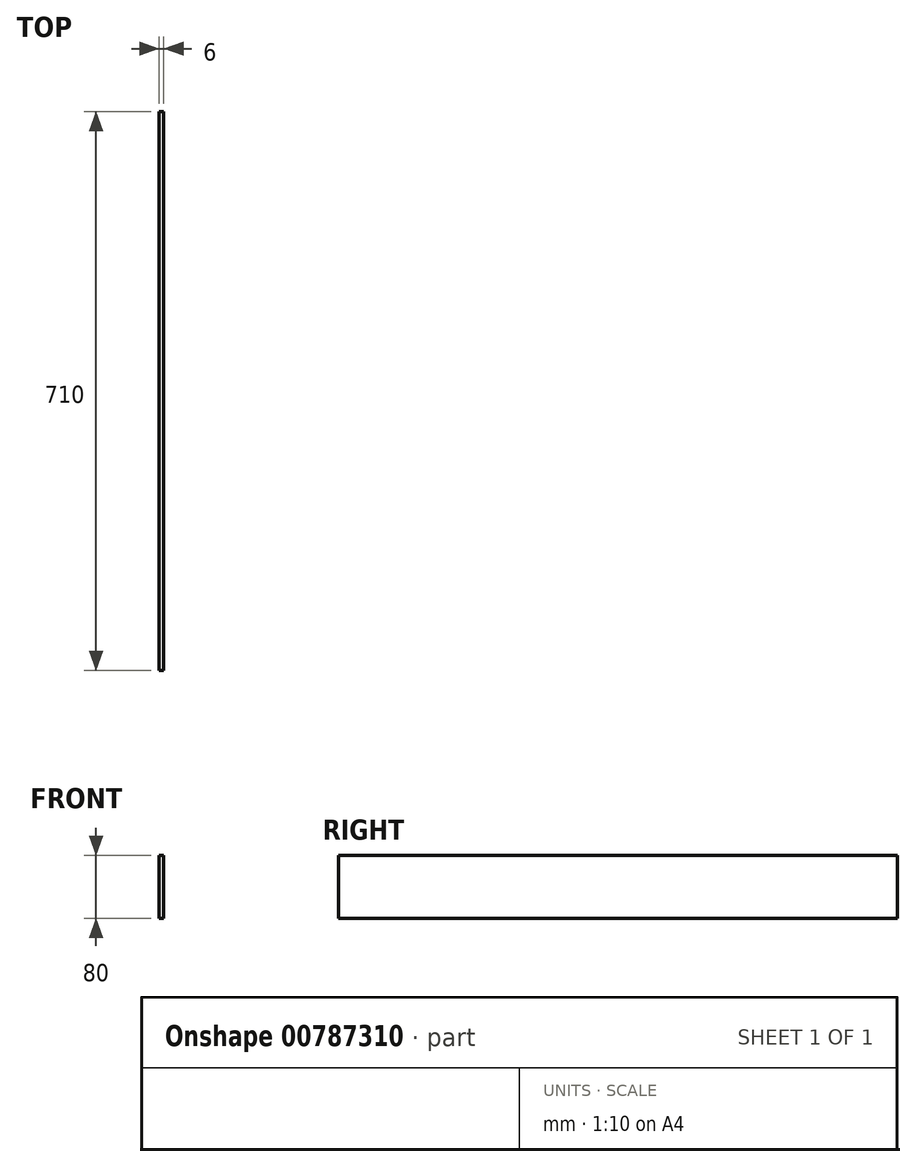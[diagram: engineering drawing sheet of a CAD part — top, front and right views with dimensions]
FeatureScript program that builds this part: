
annotation { "Feature Type Name" : "Feature", "Feature Type Description" : "" }
export const myFeature = defineFeature(function(context is Context, id is Id, definition is map)
    precondition{}
    {
        {
            var Q0;
            Q0=qCreatedBy(makeId("Front.planeOp"),FACE);
            var sketch = newSketch(context, id + "F0", { "sketchPlane" : qUnion([Q0])});
            skLineSegment(sketch, "E0.bottom", {"start": v(3, 40) * mm, "end": v(-3, 40) * mm});
            skLineSegment(sketch, "E0.top", {"start": v(3, -40) * mm, "end": v(-3, -40) * mm});
            skLineSegment(sketch, "E0.left", {"start": v(3, 40) * mm, "end": v(3, -40) * mm});
            skLineSegment(sketch, "E0.right", {"start": v(-3, 40) * mm, "end": v(-3, -40) * mm});
            skPoint(sketch, "E0.middle", {"position": v(0, 0) * mm});
            skSolve(sketch);
        }
        {
            var Q0;
            Q0=makeQuery(id+"F0.imprint","IMPRINT",FACE,{"disambiguationData":[TD([[makeQuery(id+"F0.imprint","IMPRINT",EDGE,{"derivedFrom":sQuery(id+"F0.wireOp",EDGE,"E0.bottom")}),1.0]])]});
            extrude(context, id + "F1", {"entities" : qUnion([Q0]), "depth" : 710 * mm, "offsetDistance" : 25 * mm});
        }
    });
